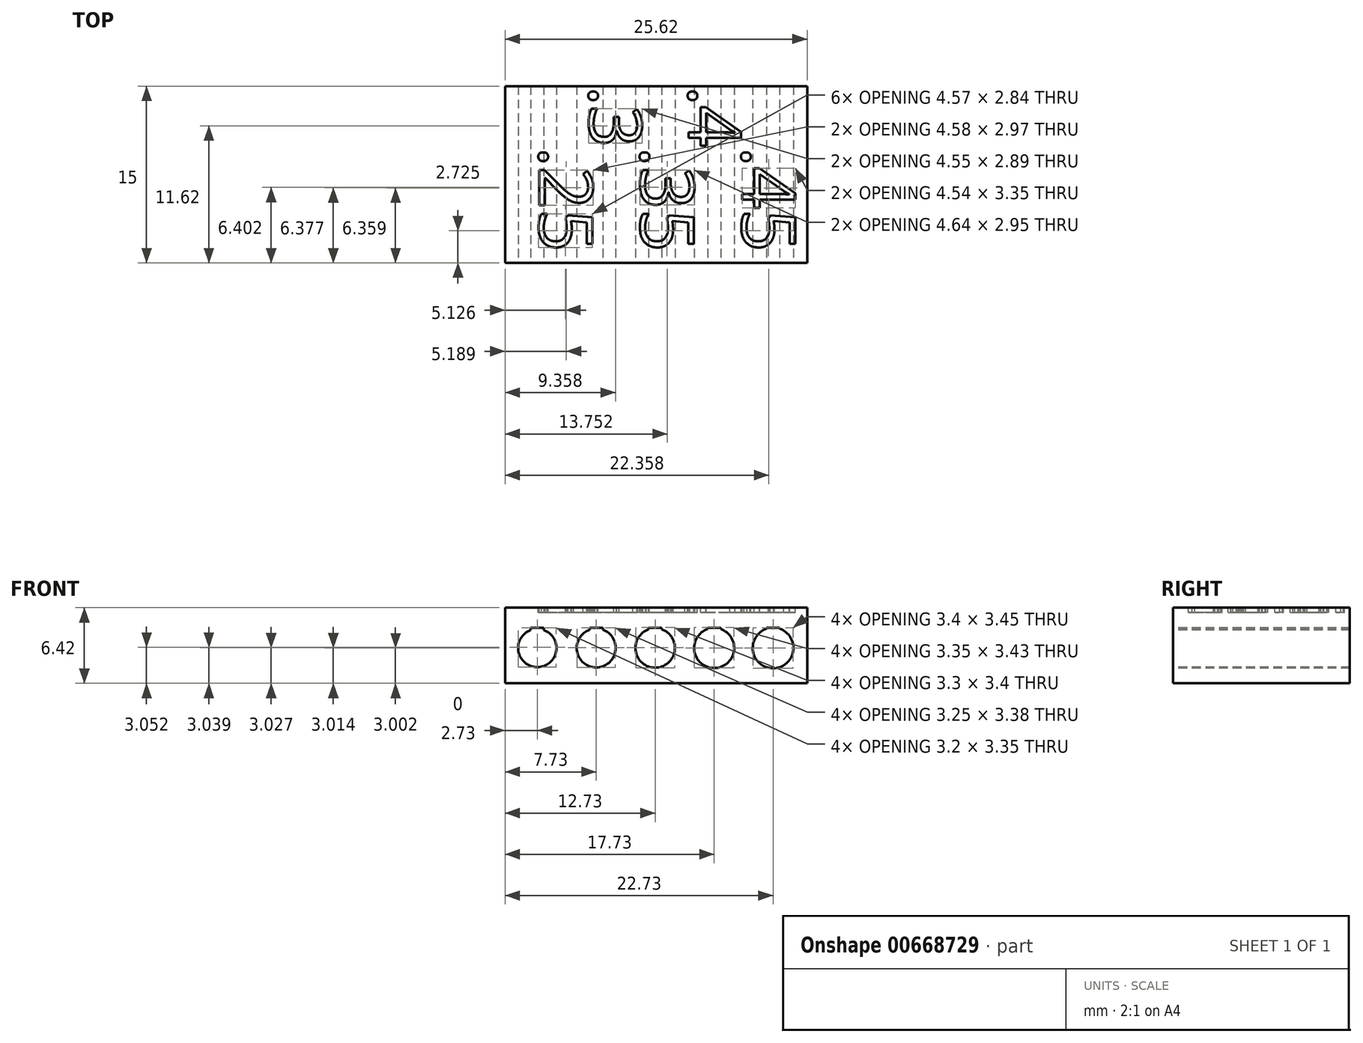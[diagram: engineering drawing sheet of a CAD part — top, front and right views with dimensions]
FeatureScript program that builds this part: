
annotation { "Feature Type Name" : "Feature", "Feature Type Description" : "" }
export const myFeature = defineFeature(function(context is Context, id is Id, definition is map)
    precondition{}
    {
        {
            var Q0;
            Q0=qCreatedBy(makeId("Front.planeOp"),FACE);
            var sketch = newSketch(context, id + "F0", { "sketchPlane" : qUnion([Q0])});
            skLineSegment(sketch, "E0", {"start": v(-9.86, 3) * mm, "end": v(19.99, 3) * mm, "construction": true});
            skCircle(sketch, "E1", {"center": v(0, 3) * mm, "radius": 1.63 * mm});
            skCircle(sketch, "E2.1.0.0", {"center": v(5, 3) * mm, "radius": 1.65 * mm});
            skCircle(sketch, "E2.2.0.0", {"center": v(10, 3) * mm, "radius": 1.68 * mm});
            skCircle(sketch, "E2.3.0.0", {"center": v(15, 3) * mm, "radius": 1.7 * mm});
            skCircle(sketch, "E2.4.0.0", {"center": v(20, 3) * mm, "radius": 1.73 * mm});
            skLineSegment(sketch, "E2.direction1", {"start": v(0, 3) * mm, "end": v(5, 3) * mm, "construction": true});
            skLineSegment(sketch, "E3.bottom", {"start": v(-2.73, 0) * mm, "end": v(22.9, 0) * mm});
            skLineSegment(sketch, "E3.top", {"start": v(-2.73, 6.42) * mm, "end": v(22.9, 6.42) * mm});
            skLineSegment(sketch, "E3.left", {"start": v(-2.73, 0) * mm, "end": v(-2.73, 6.42) * mm});
            skLineSegment(sketch, "E3.right", {"start": v(22.9, 0) * mm, "end": v(22.9, 6.42) * mm});
            skLineSegment(sketch, "E4.bottom", {"start": v(-0.55, 4.53) * mm, "end": v(0.55, 4.53) * mm});
            skLineSegment(sketch, "E4.top", {"start": v(-0.55, 4.73) * mm, "end": v(0.55, 4.73) * mm});
            skLineSegment(sketch, "E4.left", {"start": v(-0.55, 4.53) * mm, "end": v(-0.55, 4.73) * mm});
            skLineSegment(sketch, "E4.right", {"start": v(0.55, 4.53) * mm, "end": v(0.55, 4.73) * mm});
            skLineSegment(sketch, "E5.1.0.0", {"start": v(5.55, 4.53) * mm, "end": v(5.55, 4.73) * mm});
            skLineSegment(sketch, "E5.1.0.1", {"start": v(4.45, 4.53) * mm, "end": v(5.55, 4.53) * mm});
            skLineSegment(sketch, "E5.1.0.2", {"start": v(4.45, 4.73) * mm, "end": v(5.55, 4.73) * mm});
            skLineSegment(sketch, "E5.1.0.3", {"start": v(4.45, 4.53) * mm, "end": v(4.45, 4.73) * mm});
            skLineSegment(sketch, "E5.2.0.0", {"start": v(10.55, 4.53) * mm, "end": v(10.55, 4.73) * mm});
            skLineSegment(sketch, "E5.2.0.1", {"start": v(9.45, 4.53) * mm, "end": v(10.55, 4.53) * mm});
            skLineSegment(sketch, "E5.2.0.2", {"start": v(9.45, 4.73) * mm, "end": v(10.55, 4.73) * mm});
            skLineSegment(sketch, "E5.2.0.3", {"start": v(9.45, 4.53) * mm, "end": v(9.45, 4.73) * mm});
            skLineSegment(sketch, "E5.3.0.0", {"start": v(15.55, 4.53) * mm, "end": v(15.55, 4.73) * mm});
            skLineSegment(sketch, "E5.3.0.1", {"start": v(14.45, 4.53) * mm, "end": v(15.55, 4.53) * mm});
            skLineSegment(sketch, "E5.3.0.2", {"start": v(14.45, 4.73) * mm, "end": v(15.55, 4.73) * mm});
            skLineSegment(sketch, "E5.3.0.3", {"start": v(14.45, 4.53) * mm, "end": v(14.45, 4.73) * mm});
            skLineSegment(sketch, "E5.4.0.0", {"start": v(20.55, 4.53) * mm, "end": v(20.55, 4.73) * mm});
            skLineSegment(sketch, "E5.4.0.1", {"start": v(19.45, 4.53) * mm, "end": v(20.55, 4.53) * mm});
            skLineSegment(sketch, "E5.4.0.2", {"start": v(19.45, 4.73) * mm, "end": v(20.55, 4.73) * mm});
            skLineSegment(sketch, "E5.4.0.3", {"start": v(19.45, 4.53) * mm, "end": v(19.45, 4.73) * mm});
            skLineSegment(sketch, "E5.direction1", {"start": v(-0.55, 4.53) * mm, "end": v(4.45, 4.53) * mm, "construction": true});
            skSolve(sketch);
        }
        {
            var Q0;
            Q0=makeQuery(id+"F0.imprint","IMPRINT",FACE,{"disambiguationData":[TD([[makeQuery(id+"F0.imprint","IMPRINT",EDGE,{"derivedFrom":sQuery(id+"F0.wireOp",EDGE,"E3.bottom")}),1.0]])]});
            extrude(context, id + "F1", {"entities" : qUnion([Q0]), "oppositeDirection" : true, "depth" : 15 * mm, "offsetDistance" : 25 * mm});
        }
        {
            var Q0;
            Q0=makeQuery(id+"F1.opExtrude","SWEPT_FACE",FACE,{"disambiguationData":[OSD([sQuery(id+"F0.wireOp",EDGE,"E3.top")])]});
            var sketch = newSketch(context, id + "F2", { "sketchPlane" : qUnion([Q0])});
            skText(sketch, "E6", { "text": ".45\n.35\n.25\n", "fontName": "OpenSans-Regular.ttf"});
            skText(sketch, "E7", { "text": ".4\n.3", "fontName": "OpenSans-Regular.ttf"});
            const initialGuessF2  = {"E6": [0.01736, 0.00985, 0, -1, 0.00455], "E7": [0.01284, 0.015, 0, -1, 0.00446]};
            skSetInitialGuess(sketch, initialGuessF2);
            skSolve(sketch);
        }
        {
            var Q0;
            Q0 = qSketchRegion(id + "F2", true);
            extrude(context, id + "F3", {"entities" : qUnion([Q0]), "operationType" : NewBodyOperationType.REMOVE, "oppositeDirection" : true, "depth" : 0.4 * mm, "offsetDistance" : 25 * mm});
        }
    });
